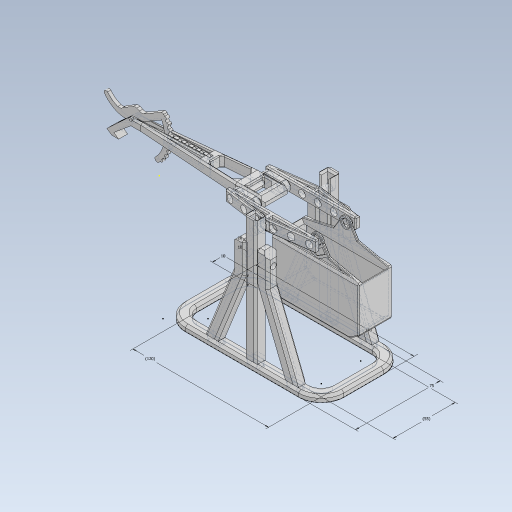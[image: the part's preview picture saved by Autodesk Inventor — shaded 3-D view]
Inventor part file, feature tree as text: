
AUTODESK INVENTOR PART (.ipt)
format: ipt  version: 2023 (Build 270158030, 158C)  size: 2,075,136 bytes
history: native  units: mm
features: extrude x39, sketch x36, chamfer x36, other x22, projected_geometry x16, mirror x11, fillet x10, plane x5, pattern_circular x2
ambient origin geometry x8: Origin, YZ Plane, XZ Plane, XY Plane, X Axis, Y Axis, Z Axis, Center Point
bodies: SOLID_WEIGHT (feature_tree)
feature tree (177):
  other  "baseplate"
  sketch  "Sketch1"  dims[d0=75.0mm d1=140.0mm]
  extrude  "Extrusion1"  Depth=140.0mm
  extrude  "Extrusion2"  Depth=10.0mm
  sketch  "Sketch3"  dims[d4=20.0mm d5=5.0mm d6=0.0mm]
  extrude  "Extrusion5"  Depth=5.0mm TaperAngle=0.0deg
  extrude  "Extrusion6"  Depth=2.0mm
  extrude  "Extrusion3"  Depth=3.0mm
  extrude  "Extrusion7"  Depth=10.0mm
  extrude  "Extrusion9"  TaperAngle=0.0deg  [1 undecoded]
  extrude  "Extrusion10"  Depth=120.0mm
  extrude  "Extrusion11"  Depth=0.01mm
  extrude  "Extrusion29"  Depth=10.0mm
  other  "center-mirror-plane"
  other  "Work Point1"
  plane  "Work Plane2"
  extrude  "Extrusion12"  Depth=25.0mm
  extrude  "Extrusion13"  Depth=5.0mm TaperAngle=0.0deg
  extrude  "Extrusion14"  Depth=10.0mm
  extrude  "Extrusion15"  Depth=10.0mm TaperAngle=0.0deg
  extrude  "Extrusion30"  Depth=5.0mm
  extrude  "Extrusion31"  Depth=6.5mm
  plane  "Work Plane5"
  extrude  "Extrusion32"  Depth=1.75mm
  extrude  "Extrusion33"  Depth=6.5mm
  extrude  "Extrusion34"  Depth=10.0mm
  fillet  "Fillet4"  Radius=3.2mm
  chamfer  "Chamfer37"  Distance=10.0mm
  extrude  "Extrusion35"  Depth=4.0mm
  chamfer  "Chamfer38"  [1 undecoded]
  fillet  "Fillet11"  Radius=21.0mm
  chamfer  "Chamfer39"  [1 undecoded]
  fillet  "Fillet12"  Radius=6.0mm
  extrude  "Extrusion36"  Depth=1.2mm
  fillet  "Fillet5"  Radius=10.0mm
  extrude  "Extrusion37"  Depth=1.2mm TaperAngle=45.0deg
  sketch  "Sketch51"  dims[d109=12.0mm d110=0.0mm d111=0.0mm d119=6.0mm d120=5.0mm d121=10.0mm d122=0.0mm d126=1.0mm d127=2.0mm d128=45.0deg d129=1.0mm d130=2.0mm d131=45.0deg d132=1.0mm d133=2.0mm d134=45.0deg d135=1.5mm d136=2.0mm d137=45.0deg d138=2.5mm d139=2.8mm d140=12.0mm d141=0.0mm d142=0.0mm d144=6.0mm d145=2.0mm d146=2.0mm d147=45.0deg d155=1.0mm d156=2.0mm d157=45.0deg d158=1.5mm d159=2.0mm d160=45.0deg d162=1.5mm d163=2.0mm d164=45.0deg d165=2.0mm d166=2.0mm d167=45.0deg d168=1.5mm d169=2.0mm d170=45.0deg d172=2.0mm d173=8.0mm d174=5.0mm d175=28.0mm d176=6.0mm d177=40.0mm d178=5.0mm d179=28.0mm d180=8.0mm d181=8.0mm d182=2.0mm d183=2.0mm d184=0.0mm d185=2.0mm d186=0.0mm d187=1.5mm d188=0.0mm d189=1.5mm d190=2.0mm d191=45.0deg d195=1.0mm d196=1.5mm d197=0.0mm d200=1.0mm d201=2.0mm d202=45.0deg d209=0.5mm d210=2.0mm d211=45.0deg d212=0.5mm d213=2.0mm d214=45.0deg d221=0.0mm d222=0.0mm d223=1.0mm d224=1.0mm d227=0.0mm d228=0.0mm d232=4.0mm d233=2.0mm d234=45.0deg d235=1.0mm d236=2.0mm d237=45.0deg d238=1.2mm d239=2.0mm d240=45.0deg d241=1.2mm d242=3.0mm d247=2.0mm d248=2.0mm d249=2.0mm d250=0.9mm d252=20.0mm d254=15.996982mm d255=8.0mm d256=6.0mm d257=6.0mm d258=6.0mm d259=5.0mm d260=5.0mm d261=14.0mm d262=14.0mm d263=0.0mm d264=0.0mm d271=3.5mm d272=2.0mm d273=45.0deg d274=3.5mm d275=2.0mm d276=45.0deg d287=1.5mm d288=2.0mm d289=45.0deg d290=1.9mm d291=10.0mm d292=0.0mm d298=3.0mm d299=0.5mm d300=0.0mm d303=3.5mm d304=3.0mm d305=0.5mm d306=0.0mm d307=2.0mm d308=2.0mm d309=0.95mm d310=0.0mm d311=0.0mm d312=5.0mm d313=10.0mm d314=0.8mm d315=27.1mm d316=3.2mm d317=0.0mm d319=0.0mm d320=0.0mm d321=36.0mm d322=0.4mm d323=0.4mm d324=3.5mm d328=3.2mm d329=0.0mm d330=2.0mm d331=4.0mm d336=6.0mm d337=3.2mm d338=0.0mm d342=3.2mm d343=3.2mm d344=3.2mm d345=3.2mm d346=3.2mm d347=3.2mm d348=3.2mm d349=3.2mm d350=3.2mm d351=1.9mm d352=0.0mm d353=4.0mm d363=19.6mm d364=19.5mm d366=3.0mm d367=90.0deg d368=23.0mm d377=10.0mm d386=2.9mm d387=0.0mm d394=1.7mm d395=1.5mm d396=4.4mm d398=3.5mm d399=2.0mm d400=45.0deg d401=3.0mm d402=2.0mm d403=45.0deg d404=4.0mm d405=1.8mm d406=2.0mm d407=45.0deg d408=4.0mm d415=4.0mm d426=1.5mm d431=7.0mm d432=0.0mm d433=0.0mm d434=4.0mm d435=2.0mm d436=2.0mm d437=45.0deg d438=1.0mm d439=2.4mm d440=0.0mm d441=0.8mm d442=2.5mm d443=2.5mm d444=1.5mm d445=1.5mm d446=3.0mm d447=14.0mm d448=14.0mm d449=14.0mm d450=10.0mm d451=0.0mm d452=1.5mm d453=1.5mm d454=4.0mm d455=0.0mm d456=2.0mm d457=2.0mm d458=45.0deg d459=3.0mm d460=2.0mm d461=45.0deg d462=1.0mm d463=2.0mm d464=45.0deg d465=12.0mm d466=12.0mm d467=5.0mm d468=25.0mm d469=5.0mm d470=3.0mm d471=0.8mm d472=2.0mm d473=45.0deg d474=1.5mm d475=0.15mm d476=5.0mm d477=0.0mm d478=0.6mm d479=2.0mm d480=45.0deg d481=5.0mm d483=38.5mm d484=38.5mm d485=2.5mm d491=2.0mm d492=30.0deg d493=14.0mm d494=0.5mm d495=2.0mm d496=45.0deg d497=2.5mm d498=2.5mm d499=30.0deg d500=1.5mm d501=0.0mm d505=11.0mm d506=5.0mm d507=2.0mm d508=45.0deg d509=6.981317mm d510=75.0deg d511=20.0mm d512=0.4mm d514=10.293981mm d520=1.5mm d521=63.0mm d522=3.2mm d523=30.0deg d524=4.0mm d525=75.0deg d526=35.0mm d527=5.072433mm d528=2.3mm d529=4.5mm d530=1.2mm d531=2.9mm d532=0.0mm d533=1.5mm d534=0.0mm d535=0.0mm d542=40.0mm d543=4.363323mm d545=50.0mm d546=5.759587mm d548=5.5mm d549=38.0mm d550=10.902886mm d551=5.0mm d552=2.0mm d553=45.0deg d554=1.0mm d555=2.0mm d556=45.0deg d557=2.0mm d558=2.0mm d559=0.0mm d560=1.0mm d561=2.0mm d562=45.0deg d563=1.9mm d564=2.0mm d565=45.0deg d566=1.6mm d567=2.0mm d568=45.0deg]
  extrude  "Extrusion45"  Depth=1.2mm TaperAngle=45.0deg
  extrude  "Extrusion46"  Depth=1.2mm TaperAngle=45.0deg
  pattern_circular  "Circular Pattern3"  Angle=45.0deg  [1 undecoded]
  pattern_circular  "Circular Pattern4"  [2 undecoded]
  fillet  "Fillet13"  Radius=2.8mm
  fillet  "Fillet15"  Radius=12.0mm
  fillet  "Fillet10"  [1 undecoded]
  extrude  "Extrusion17"  Depth=1.2mm
  extrude  "Extrusion26"  Depth=1.2mm TaperAngle=45.0deg
  extrude  "Extrusion38"  Depth=1.2mm TaperAngle=45.0deg
  fillet  "Fillet16"  Radius=1.5mm
  chamfer  "Chamfer1"  Distance=1.5mm Angle=45.0deg
  chamfer  "Chamfer2"  Distance=2.0mm Angle=45.0deg
  chamfer  "Chamfer3"  Distance=1.5mm Angle=45.0deg
  chamfer  "Chamfer4"  Distance=2.0mm
  extrude  "Extrusion19"  Depth=1.2mm
  chamfer  "Chamfer5"  Distance=5.0mm
  chamfer  "Chamfer8"  Distance=28.0mm
  chamfer  "Chamfer9"  Distance=6.0mm
  chamfer  "Chamfer10"  Distance=40.0mm
  chamfer  "Chamfer43"  Distance=5.0mm
  extrude  "Extrusion39"  Depth=1.2mm
  mirror  "Mirror12"
  chamfer  "Chamfer11"  Distance=8.0mm
  chamfer  "Chamfer50"  Distance=8.0mm
  chamfer  "Chamfer12"  Distance=2.0mm
  plane  "Work Plane4"
  extrude  "CW-extrusion"  Depth=1.2mm TaperAngle=0.0deg
  mirror  "Mirror3"
  extrude  "Extrusion21"  Depth=1.2mm TaperAngle=0.0deg
  extrude  "Extrusion22"  Depth=1.2mm TaperAngle=0.0deg
  mirror  "Mirror4"
  chamfer  "Chamfer13"  Distance=1.5mm Angle=45.0deg
  extrude  "Extrusion23"  Depth=1.2mm TaperAngle=0.0deg
  mirror  "Mirror5"
  chamfer  "Chamfer31"  Distance=1.0mm Angle=45.0deg
  chamfer  "Chamfer14"  Distance=0.5mm Angle=45.0deg
  chamfer  "Chamfer17"  Distance=0.5mm Angle=45.0deg
  chamfer  "Chamfer18"  [1 undecoded]
  extrude  "Extrusion24"  Depth=1.2mm
  extrude  "Extrusion25"  Depth=1.2mm
  chamfer  "Chamfer20"  [1 undecoded]
  chamfer  "Chamfer49"  Distance=4.0mm Angle=45.0deg
  chamfer  "Chamfer21"  Distance=1.0mm Angle=45.0deg
  extrude  "Extrusion40"  Depth=1.2mm TaperAngle=45.0deg
  extrude  "Extrusion41"  Depth=1.2mm
  chamfer  "Chamfer22"  Distance=3.0mm
  chamfer  "Chamfer44"  Distance=2.0mm
  chamfer  "Chamfer45"  Distance=2.0mm
  chamfer  "Chamfer46"  Distance=2.0mm
  fillet  "Fillet3"  Radius=0.9mm
  mirror  "Mirror2"
  mirror  "Mirror1"
  plane  "Work Plane3"
  mirror  "Mirror6"
  mirror  "Mirror7"
  mirror  "Mirror8"
  chamfer  "Chamfer26"  Distance=20.0mm
  chamfer  "Chamfer27"  Distance=15.996982mm
  extrude  "Extrusion43"  Depth=1.2mm
  mirror  "Mirror10"
  chamfer  "Chamfer47"  Distance=6.0mm
  extrude  "Extrusion42"  Depth=1.2mm
  chamfer  "Chamfer48"  Distance=6.0mm
  mirror  "Mirror11"
  sketch  "Sketch35"  dims[d79=40.0mm]
  plane  "Work Plane6"
  chamfer  "Chamfer51"  Distance=5.0mm
  chamfer  "Chamfer52"  Distance=5.0mm
  fillet  "Fillet17"  Radius=14.0mm
  chamfer  "Chamfer53"  Distance=14.0mm
  chamfer  "Chamfer54"  [1 undecoded]
  chamfer  "Chamfer55"  Distance=3.5mm Angle=45.0deg
  sketch  "Sketch2"  dims[d2=10.0mm d3=10.0mm]
  sketch  "Sketch4"  dims[d7=6.0mm d9=2.0mm]
  projected_geometry  "Projected Loop1"
  other  "A-frame"
  sketch  "Sketch7"  dims[d10=10.0mm d11=3.0mm]
  projected_geometry  "Projected Loop2"
  other  "upright"
  projected_geometry  "Projected Loop3"
  sketch  "Sketch10"  dims[d12=1.75mm d13=6.0mm d14=10.0mm]
  sketch  "Sketch12"  dims[d15=60.0mm d16=0.0mm d17=0.0mm]
  sketch  "Sketch13"  dims[d18=55.0mm d19=120.0mm]
  sketch  "Sketch14"  dims[d22=0.1mm d23=0.01mm]
  other  "pivot"
  sketch  "Sketch16"  dims[d24=5.0mm d25=0.0mm d38=10.0mm]
  other  "throw-arm-top"
  sketch  "Sketch18"  dims[d39=25.0mm d40=25.0mm]
  sketch  "Sketch20"  dims[d41=0.01mm d42=5.0mm d43=5.0mm d44=0.0mm d45=0.0mm]
  sketch  "Sketch22"  dims[d47=10.0mm d50=10.0mm]
  other  "counterweight"
  projected_geometry  "Projected Loop5"
  sketch  "Sketch26"  dims[d51=110.0mm d52=0.0mm d53=10.0mm d54=0.0mm]
  projected_geometry  "Projected Loop6"
  sketch  "Sketch27"  dims[d60=5.0mm d61=5.0mm]
  projected_geometry  "Projected Loop7"
  sketch  "Sketch29"  dims[d64=0.0mm d65=0.0mm d66=6.5mm]
  sketch  "Sketch30"  dims[d67=1.75mm d68=1.75mm]
  other  "Pattern of pivot:1"
  other  "pivot-mirror"
  other  "Pattern of upright:2"
  other  "upright-mirror"
  other  "Pattern of A-frame:3"
  other  "A-frame-b"
  other  "Pattern of A-frame:4"
  other  "A-frame-c"
  other  "Pattern of A-frame-b:5"
  other  "A-frame-d"
  sketch  "Sketch31"  dims[d69=11.0mm d70=6.5mm]
  projected_geometry  "Projected Loop8"
  sketch  "Sketch32"  dims[d71=7.0mm d72=0.0mm d73=6.0mm d74=3.2mm d75=10.0mm d76=0.0mm]
  projected_geometry  "Projected Loop9"
  sketch  "Sketch34"  dims[d77=4.0mm d78=40.0mm]
  sketch  "Sketch36"  dims[d80=5.0mm]
  sketch  "Sketch37"  dims[d83=4.0mm]
  sketch  "Sketch38"  dims[d84=29.0mm]
  projected_geometry  "Projected Loop15"
  projected_geometry  "Projected Loop16"
  sketch  "Sketch39"  dims[d85=2.0mm d86=8.0mm d87=0.0mm d88=0.0mm]
  sketch  "Sketch40"  dims[d89=6.0mm]
  projected_geometry  "Projected Loop17"
  sketch  "Sketch41"  dims[d90=5.0mm]
  sketch  "Sketch42"  dims[d91=5.0mm d92=0.0mm d93=0.0mm d96=21.0mm]
  sketch  "Sketch43"  dims[d99=8.0mm]
  other  "ratchet"
  sketch  "Sketch44"  dims[d100=10.0mm]
  sketch  "Sketch45"  dims[d101=6.5mm]
  projected_geometry  "Projected Loop18"
  projected_geometry  "Projected Loop19"
  sketch  "Sketch46"  dims[d102=6.5mm]
  sketch  "Sketch47"  dims[d103=125.0mm]
  projected_geometry  "Projected Loop20"
  sketch  "Sketch48"  dims[d104=10.0mm d105=5.0mm d106=0.0mm d107=0.0mm]
  other  "spacer-a"
  other  "Pattern of spacer-a:6"
  other  "spacer-b"
  projected_geometry  "Projected Loop24"
  sketch  "Sketch49"  dims[d108=7.0mm]
  projected_geometry  "Projected Loop25"
note: 10 required parameter values undecoded (feature->parameter linkage not recoverable at this tier; creation-order binding heuristic only, values carry confidence <= 0.55)
